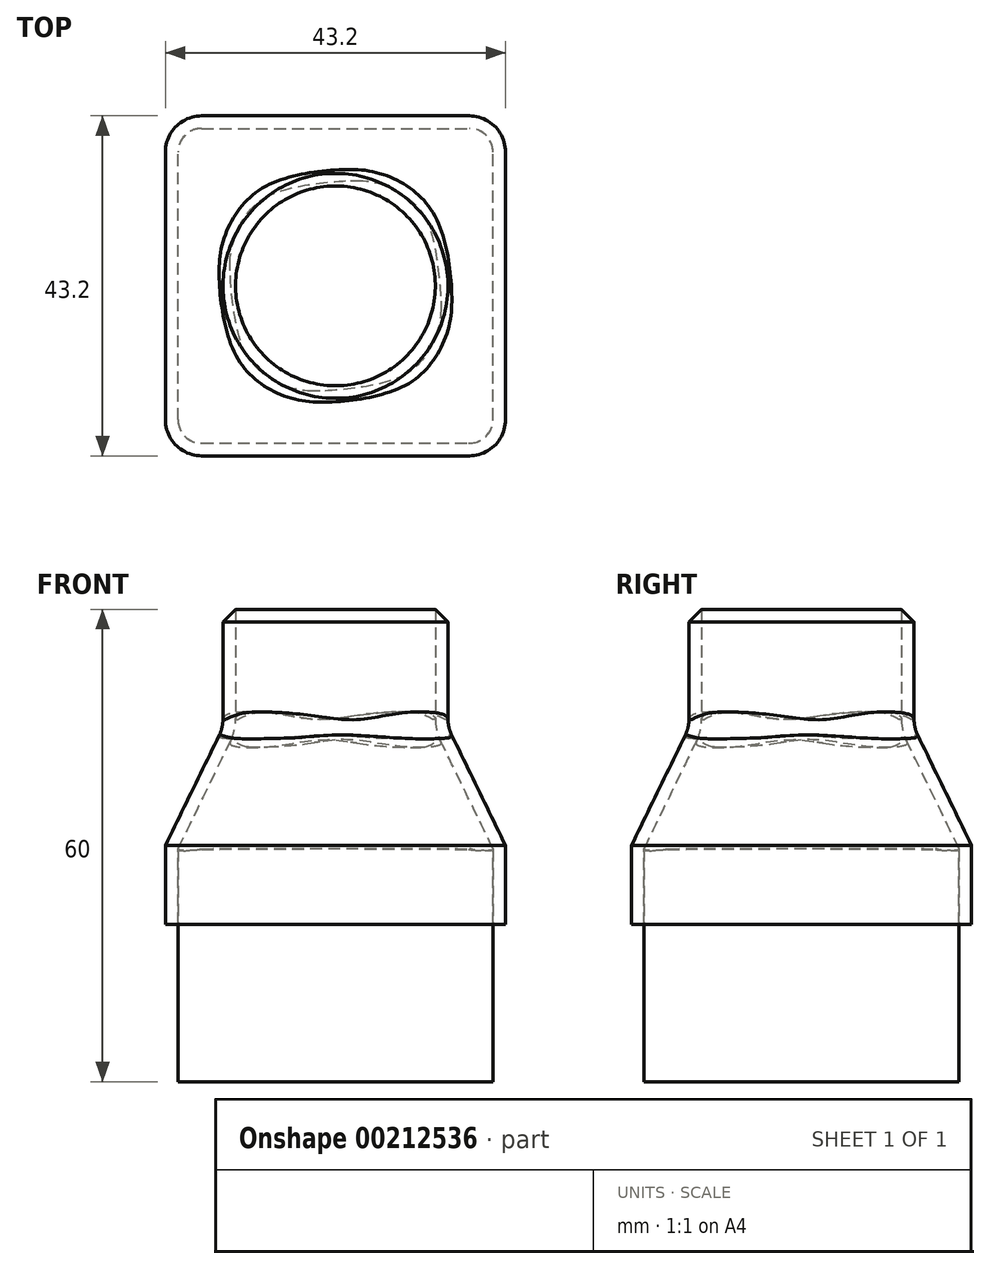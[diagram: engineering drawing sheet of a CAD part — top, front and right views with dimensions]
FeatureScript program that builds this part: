
annotation { "Feature Type Name" : "Feature", "Feature Type Description" : "" }
export const myFeature = defineFeature(function(context is Context, id is Id, definition is map)
    precondition{}
    {
        {
            var Q0;
            Q0=qCreatedBy(makeId("Top.planeOp"),FACE);
            var sketch = newSketch(context, id + "F0", { "sketchPlane" : qUnion([Q0])});
            skLineSegment(sketch, "E0.bottom", {"start": v(3, 0) * mm, "end": v(37, 0) * mm});
            skLineSegment(sketch, "E0.top", {"start": v(3, 40) * mm, "end": v(37, 40) * mm});
            skLineSegment(sketch, "E0.left", {"start": v(0, 3) * mm, "end": v(0, 37) * mm});
            skLineSegment(sketch, "E0.right", {"start": v(40, 3) * mm, "end": v(40, 37) * mm});
            skPoint(sketch, "E1.visualSharp", {"position": v(40, 40) * mm});
            skArc(sketch, "E1.filletArc", {"start": v(40, 37) * mm, "mid": v(39.12, 39.12) * mm, "end": v(37, 40) * mm});
            skPoint(sketch, "E2.visualSharp", {"position": v(0, 0) * mm});
            skArc(sketch, "E2.filletArc", {"start": v(0, 3) * mm, "mid": v(0.88, 0.88) * mm, "end": v(3, 0) * mm});
            skPoint(sketch, "E3.visualSharp", {"position": v(0, 40) * mm});
            skArc(sketch, "E3.filletArc", {"start": v(3, 40) * mm, "mid": v(0.88, 39.12) * mm, "end": v(0, 37) * mm});
            skPoint(sketch, "E4.visualSharp", {"position": v(40, 0) * mm});
            skArc(sketch, "E4.filletArc", {"start": v(37, 0) * mm, "mid": v(39.12, 0.88) * mm, "end": v(40, 3) * mm});
            skArc(sketch, "E5.0", {"start": v(37, -1.6) * mm, "mid": v(40.25, -0.25) * mm, "end": v(41.6, 3) * mm});
            skLineSegment(sketch, "E5.1", {"start": v(3, -1.6) * mm, "end": v(37, -1.6) * mm});
            skLineSegment(sketch, "E5.2", {"start": v(41.6, 3) * mm, "end": v(41.6, 37) * mm});
            skArc(sketch, "E5.3", {"start": v(-1.6, 3) * mm, "mid": v(-0.25, -0.25) * mm, "end": v(3, -1.6) * mm});
            skArc(sketch, "E5.4", {"start": v(41.6, 37) * mm, "mid": v(40.25, 40.25) * mm, "end": v(37, 41.6) * mm});
            skLineSegment(sketch, "E5.5", {"start": v(3, 41.6) * mm, "end": v(37, 41.6) * mm});
            skArc(sketch, "E5.6", {"start": v(3, 41.6) * mm, "mid": v(-0.25, 40.25) * mm, "end": v(-1.6, 37) * mm});
            skLineSegment(sketch, "E5.7", {"start": v(-1.6, 3) * mm, "end": v(-1.6, 37) * mm});
            skSolve(sketch);
        }
        {
            var Q0;
            Q0=makeQuery(id+"F0.imprint","IMPRINT",FACE,{"disambiguationData":[TD([[makeQuery(id+"F0.imprint","IMPRINT",EDGE,{"derivedFrom":sQuery(id+"F0.wireOp",EDGE,"E0.bottom")}),-1.0]])]});
            var Q1;
            Q1=makeQuery(id+"F0.imprint","IMPRINT",FACE,{"disambiguationData":[TD([[makeQuery(id+"F0.imprint","IMPRINT",EDGE,{"derivedFrom":sQuery(id+"F0.wireOp",EDGE,"E0.bottom")}),1.0]])]});
            extrude(context, id + "F1", {"entities" : qUnion([Q0, Q1]), "depth" : 10 * mm});
        }
        {
            var Q0;
            Q0=makeQuery(id+"F1.opExtrude","CAP_FACE",FACE,{"disambiguationData":[OSD([sQuery(id+"F0.wireOp",EDGE,"E0.bottom"),sQuery(id+"F0.wireOp",EDGE,"E0.top"),sQuery(id+"F0.wireOp",EDGE,"E0.left"),sQuery(id+"F0.wireOp",EDGE,"E0.right"),sQuery(id+"F0.wireOp",EDGE,"E1.filletArc"),sQuery(id+"F0.wireOp",EDGE,"E2.filletArc"),sQuery(id+"F0.wireOp",EDGE,"E3.filletArc"),sQuery(id+"F0.wireOp",EDGE,"E4.filletArc"),sQuery(id+"F0.wireOp",EDGE,"E5.0"),sQuery(id+"F0.wireOp",EDGE,"E5.1"),sQuery(id+"F0.wireOp",EDGE,"E5.2"),sQuery(id+"F0.wireOp",EDGE,"E5.3"),sQuery(id+"F0.wireOp",EDGE,"E5.4"),sQuery(id+"F0.wireOp",EDGE,"E5.5"),sQuery(id+"F0.wireOp",EDGE,"E5.6"),sQuery(id+"F0.wireOp",EDGE,"E5.7")])],"isStart":false});
            cPlane(context, id + "F2", {"entities" : qUnion([Q0]), "cplaneType" : CPlaneType.OFFSET, "offset" : 15 * mm, "width" : 150 * mm, "height" : 150 * mm});
        }
        {
            var Q0;
            Q0=qCreatedBy(id+"F2.planeOp",FACE);
            var sketch = newSketch(context, id + "F3", { "sketchPlane" : qUnion([Q0])});
            skLineSegment(sketch, "E6", {"start": v(-1.6, 20) * mm, "end": v(41.6, 20) * mm, "construction": true});
            skCircle(sketch, "E7", {"center": v(20, 20) * mm, "radius": 14.29 * mm});
            skCircle(sketch, "E8", {"center": v(20, 20) * mm, "radius": 12.69 * mm, "construction": true});
            skPoint(sketch, "E9.0", {"position": v(41.6, 20) * mm});
            skPoint(sketch, "E10.1", {"position": v(-1.6, 20) * mm});
            skSolve(sketch);
        }
        {
            var Q1;
            Q1=makeQuery(id+"F1.opExtrude","CAP_FACE",FACE,{"disambiguationData":[OSD([sQuery(id+"F0.wireOp",EDGE,"E5.0"),sQuery(id+"F0.wireOp",EDGE,"E5.1"),sQuery(id+"F0.wireOp",EDGE,"E5.2"),sQuery(id+"F0.wireOp",EDGE,"E5.3"),sQuery(id+"F0.wireOp",EDGE,"E5.4"),sQuery(id+"F0.wireOp",EDGE,"E5.5"),sQuery(id+"F0.wireOp",EDGE,"E5.6"),sQuery(id+"F0.wireOp",EDGE,"E5.7")])],"isStart":false});
            var Q2;
            Q2=makeQuery(id+"F3.imprint","IMPRINT",FACE,{"disambiguationData":[TD([[makeQuery(id+"F3.imprint","IMPRINT",EDGE,{"derivedFrom":sQuery(id+"F3.wireOp",EDGE,"E7")}),1.0]])]});
            loft(context, id + "F4", {"operationType" : NewBodyOperationType.ADD, "sheetProfilesArray" : [{ "sheetProfileEntities" : qUnion([Q1]) }, { "sheetProfileEntities" : qUnion([Q2]) }]});
        }
        {
            var Q0;
            Q0=makeQuery(id+"F4.opLoft","CAP_FACE",FACE,{"disambiguationData":[OSD([makeQuery(id+"F3.imprint","IMPRINT",FACE,{"disambiguationData":[TD([[makeQuery(id+"F3.imprint","IMPRINT",EDGE,{"derivedFrom":sQuery(id+"F3.wireOp",EDGE,"E7")}),1.0]])]})])],"isStart":true});
            extrude(context, id + "F5", {"entities" : qUnion([Q0]), "operationType" : NewBodyOperationType.ADD, "depth" : 15 * mm});
        }
        {
            var Q0;
            {var subQ0=sQuery(id+"F3.wireOp",EDGE,"E7");var subQ1=sQuery(id+"F0.wireOp",EDGE,"E5.5");var subQ2=sQuery(id+"F0.wireOp",EDGE,"E5.4");var subQ3=sQuery(id+"F0.wireOp",EDGE,"E5.2");Q0=makeQuery(id+"F5.boolean.opBoolean","MERGE",EDGE,{"derivedFrom":[makeQuery(id+"F4.opLoft","MID_CAP_EDGE",EDGE,{"disambiguationData":[OSD([subQ3,subQ2,subQ1,subQ0])],"capPos":1.0}),makeQuery(id+"F5.opExtrude","CAP_EDGE",EDGE,{"disambiguationData":[OSD([subQ3,subQ2,subQ1,subQ0])],"isStart":true})]});}
            fillet(context, id + "F6", {"entities" : qUnion([Q0]), "radius" : 5 * mm, "tangentPropagation" : true, "allowEdgeOverflow" : false});
        }
        {
            var Q0;
            Q0=makeQuery(id+"F1.opExtrude","CAP_FACE",FACE,{"disambiguationData":[OSD([sQuery(id+"F0.wireOp",EDGE,"E5.0"),sQuery(id+"F0.wireOp",EDGE,"E5.1"),sQuery(id+"F0.wireOp",EDGE,"E5.2"),sQuery(id+"F0.wireOp",EDGE,"E5.3"),sQuery(id+"F0.wireOp",EDGE,"E5.4"),sQuery(id+"F0.wireOp",EDGE,"E5.5"),sQuery(id+"F0.wireOp",EDGE,"E5.6"),sQuery(id+"F0.wireOp",EDGE,"E5.7")])],"isStart":true});
            var Q1;
            Q1=makeQuery(id+"F5.opExtrude","CAP_FACE",FACE,{"disambiguationData":[OSD([makeQuery(id+"F3.imprint","IMPRINT",FACE,{"disambiguationData":[TD([[makeQuery(id+"F3.imprint","IMPRINT",EDGE,{"derivedFrom":sQuery(id+"F3.wireOp",EDGE,"E7")}),1.0]])]})])],"isStart":false});
            shell(context, id + "F7", {"entities" : qUnion([Q0, Q1]), "thickness" : 1.6 * mm});
        }
        {
            var Q0;
            Q0=makeQuery(id+"F5.opExtrude","CAP_EDGE",EDGE,{"disambiguationData":[OSD([sQuery(id+"F0.wireOp",EDGE,"E5.0"),sQuery(id+"F0.wireOp",EDGE,"E5.2"),sQuery(id+"F0.wireOp",EDGE,"E5.4"),sQuery(id+"F3.wireOp",EDGE,"E7")])],"isStart":false});
            var Q1;
            Q1=makeQuery(id+"F5.opExtrude","CAP_EDGE",EDGE,{"disambiguationData":[OSD([sQuery(id+"F0.wireOp",EDGE,"E5.2"),sQuery(id+"F0.wireOp",EDGE,"E5.4"),sQuery(id+"F0.wireOp",EDGE,"E5.5"),sQuery(id+"F3.wireOp",EDGE,"E7")])],"isStart":false});
            var Q2;
            Q2=makeQuery(id+"F5.opExtrude","CAP_EDGE",EDGE,{"disambiguationData":[OSD([sQuery(id+"F0.wireOp",EDGE,"E5.4"),sQuery(id+"F0.wireOp",EDGE,"E5.5"),sQuery(id+"F0.wireOp",EDGE,"E5.6"),sQuery(id+"F3.wireOp",EDGE,"E7")])],"isStart":false});
            var Q3;
            Q3=makeQuery(id+"F5.opExtrude","CAP_EDGE",EDGE,{"disambiguationData":[OSD([sQuery(id+"F0.wireOp",EDGE,"E5.5"),sQuery(id+"F0.wireOp",EDGE,"E5.6"),sQuery(id+"F0.wireOp",EDGE,"E5.7"),sQuery(id+"F3.wireOp",EDGE,"E7")])],"isStart":false});
            var Q4;
            Q4=makeQuery(id+"F5.opExtrude","CAP_EDGE",EDGE,{"disambiguationData":[OSD([sQuery(id+"F0.wireOp",EDGE,"E5.3"),sQuery(id+"F0.wireOp",EDGE,"E5.6"),sQuery(id+"F0.wireOp",EDGE,"E5.7"),sQuery(id+"F3.wireOp",EDGE,"E7")])],"isStart":false});
            var Q5;
            Q5=makeQuery(id+"F5.opExtrude","CAP_EDGE",EDGE,{"disambiguationData":[OSD([sQuery(id+"F0.wireOp",EDGE,"E5.0"),sQuery(id+"F0.wireOp",EDGE,"E5.1"),sQuery(id+"F0.wireOp",EDGE,"E5.3"),sQuery(id+"F0.wireOp",EDGE,"E5.7"),sQuery(id+"F3.wireOp",EDGE,"E7")])],"isStart":false});
            var Q6;
            Q6=makeQuery(id+"F5.opExtrude","CAP_EDGE",EDGE,{"disambiguationData":[OSD([sQuery(id+"F0.wireOp",EDGE,"E5.0"),sQuery(id+"F0.wireOp",EDGE,"E5.1"),sQuery(id+"F3.wireOp",EDGE,"E7")])],"isStart":false});
            var Q7;
            Q7=makeQuery(id+"F5.opExtrude","CAP_EDGE",EDGE,{"disambiguationData":[OSD([sQuery(id+"F0.wireOp",EDGE,"E5.0"),sQuery(id+"F0.wireOp",EDGE,"E5.1"),sQuery(id+"F0.wireOp",EDGE,"E5.2"),sQuery(id+"F3.wireOp",EDGE,"E7")])],"isStart":false});
            chamfer(context, id + "F8", {"entities" : qUnion([Q0, Q1, Q2, Q3, Q4, Q5, Q6, Q7]), "width" : 1.6 * mm, "tangentPropagation" : true});
        }
        {
            var Q0;
            Q0=makeQuery(id+"F1.opExtrude","CAP_FACE",FACE,{"disambiguationData":[OSD([sQuery(id+"F0.wireOp",EDGE,"E5.0"),sQuery(id+"F0.wireOp",EDGE,"E5.1"),sQuery(id+"F0.wireOp",EDGE,"E5.2"),sQuery(id+"F0.wireOp",EDGE,"E5.3"),sQuery(id+"F0.wireOp",EDGE,"E5.4"),sQuery(id+"F0.wireOp",EDGE,"E5.5"),sQuery(id+"F0.wireOp",EDGE,"E5.6"),sQuery(id+"F0.wireOp",EDGE,"E5.7")])],"isStart":true});
            var sketch = newSketch(context, id + "F9", { "sketchPlane" : qUnion([Q0])});
            skLineSegment(sketch, "E11.0", {"start": v(3, 0) * mm, "end": v(37, 0) * mm});
            skArc(sketch, "E12.0", {"start": v(0, -3) * mm, "mid": v(0.88, -0.88) * mm, "end": v(3, 0) * mm});
            skLineSegment(sketch, "E13.0", {"start": v(0, -3) * mm, "end": v(0, -37) * mm});
            skArc(sketch, "E14.0", {"start": v(3, -40) * mm, "mid": v(0.88, -39.12) * mm, "end": v(0, -37) * mm});
            skLineSegment(sketch, "E15.0", {"start": v(3, -40) * mm, "end": v(37, -40) * mm});
            skArc(sketch, "E16.0", {"start": v(40, -37) * mm, "mid": v(39.12, -39.12) * mm, "end": v(37, -40) * mm});
            skLineSegment(sketch, "E17.0", {"start": v(40, -3) * mm, "end": v(40, -37) * mm});
            skArc(sketch, "E18.0", {"start": v(37, 0) * mm, "mid": v(39.12, -0.88) * mm, "end": v(40, -3) * mm});
            skSolve(sketch);
        }
        {
            var Q0;
            Q0=makeQuery(id+"F9.imprint","IMPRINT",FACE,{"disambiguationData":[TD([[makeQuery(id+"F9.imprint","IMPRINT",EDGE,{"derivedFrom":sQuery(id+"F9.wireOp",EDGE,"E11.0")}),-1.0]])]});
            extrude(context, id + "F10", {"entities" : qUnion([Q0]), "depth" : 20 * mm});
        }
    });
